# Revit family: Shower-Valves_and_Controls-KOHLER-Beitou-K-77236IN
name_source: partatom
category: Plumbing Fixtures
revit_build: Autodesk Revit 2017 (Build: 20160225_1515(x64)
units: mm (PartAtom-declared; Revit-internal decimal feet)

## family parameters
Cut with Voids When Loaded = No
Host = Face
OmniClass Number = 23.27.31.00
OmniClass Title = Valves
Part Type = Normal
Room Calculation Point = No
Round Connector Dimension = Use Diameter
Shared = No

## types (4) — shared parameters
ADA Compliant = No
Assembly Code = D2020
CW Connection = Yes
Cold Water Inlet = Cold Water Inlet
Date Modified = 10/29/2020
Default Elevation = 47 1/4"
Description = Hi-Flow Thermostatic Valve, 4-Way
Flow Rate = 0 GPM
HW Connection = Yes
Height = 17 11/16"
Hot Water Inlet = Hot Water Inlet
Length = 6 1/4"
Manufacturer = KOHLER Co.
Master Format 2014 = 23 09 13.33
Master Format 2014 Name = Control Valves
Material = Brass Construction
Pressure = 0.00 psi
Product Documentation Link = http://resources.kohler.com
Product Name = Beitou
Product Page URL = https://www.kohler.co.in
Tempered Water Outlet 1 = Tempered Water Outlet 1
Tempered Water Outlet 2 = Tempered Water Outlet 2
Tempered Water Outlet 3 = Tempered Water Outlet 3
Tempered Water Outlet 4 = Tempered Water Outlet 4
URL = https://www.kohler.co.in
Vent Connection = No
Waste Connection = No
Waste Water Outlet = Waste Water Outlet
WaterSense Certified = No
Width = 3 5/8"

## per-type parameters (varying)
| type | Finish | Model | Type |
| BV-Brushed Bronze | Kohler-Metal-BV-Brushed_Bronze | K-77236IN-9-BV | 1 |
| BN-Vibrant Brushed Nickel | Kohler-Metal-BN-Vibrant_Brushed_Nickel | K-77236IN-9-BN | 2 |
| CP- Polished Chrome | Kohler-Metal-CP-Polished_Chrome | K-77236IN-9-CP | 3 |
| AF-Vibrant French Gold | Kohler-Metal-AF-Vibrant_French_Gold | K-77236IN-9-AF | 4 |

## geometry (parser evidence)
native form markers: Sweep x5
no freeform markers — native parametric forms only
